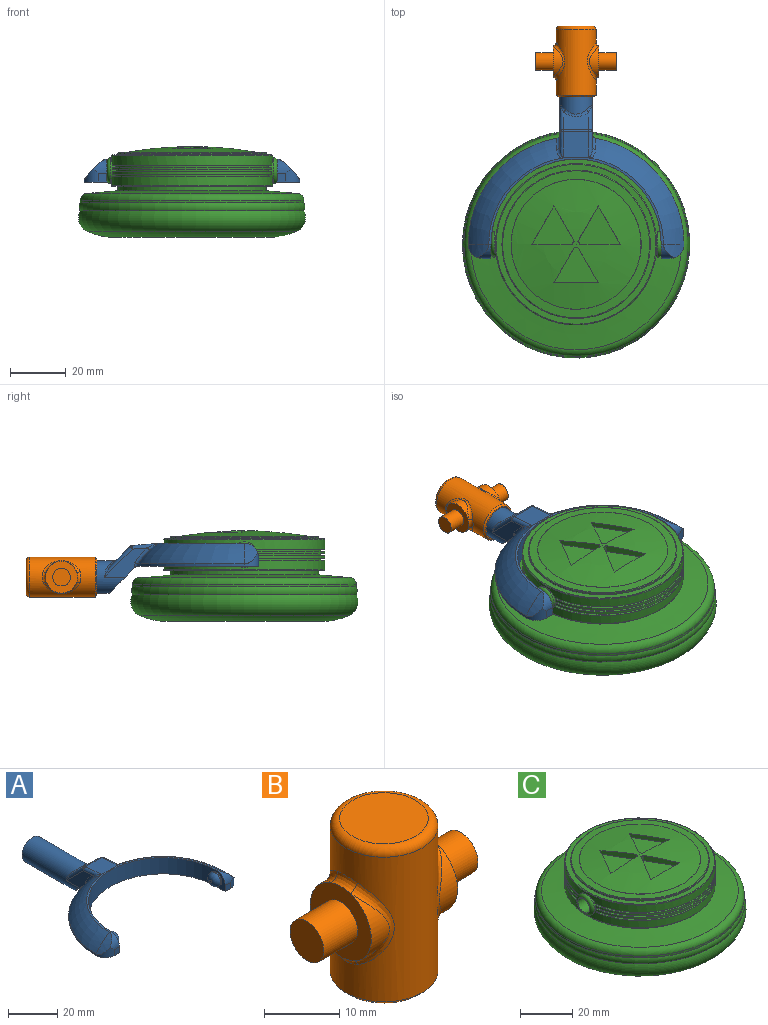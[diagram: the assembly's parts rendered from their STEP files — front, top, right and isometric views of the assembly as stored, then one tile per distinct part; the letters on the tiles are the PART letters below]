
ASSEMBLY  parts=3 mates=2
PART A: 48 faces, bbox 77.3x80.8x18.2 mm
  f0: plane 11.99x9.83mm, normal (0,-0.71,-0.71), area 141.5mm2, adj f1,f2,f9,f30,f43,f46
  f1: plane 15.39x10.49mm, normal (-1,0,0), area 63.5mm2, adj f0,f30,f32,f36,f46,f47
  f2: plane 15.39x10.49mm, normal (1,0,0), area 63.5mm2, adj f0,f30,f34,f39,f43,f44
  f3: plane 9.14x6.37mm, normal (0,0.71,0.71), area 67.6mm2, adj f35,f36,f39,f40
  f4: cylinder r=38.61mm len=37.99mm, axis (0,0,-1), area 42.6mm2, adj f6,f9,f17,f46,f47
  f5: torus R=19.3mm, axis (0,0,-1), area 507.8mm2, adj f10,f11,f12,f29,f42,f44
  f6: torus R=19.3mm, axis (0,0,-1), area 507.8mm2, adj f4,f11,f15,f28,f45,f47
  f7: cylinder r=30.48mm len=60.96mm, axis (0,0,-1), area 746.6mm2, adj f8,f9,f11,f14,f21,f24
  f8: plane 8.13x5.08mm, normal (-1,0,0), area 19.9mm2, adj f7,f9,f13,f19,f24
  f9: plane 77.22x43.73mm, normal (0,0,-1), area 956.2mm2, adj f0,f4,f7,f8,f10,f13,f14,f16
  f10: cylinder r=38.61mm len=37.99mm, axis (0,0,-1), area 42.6mm2, adj f5,f9,f20,f43,f44
  f11: plane 62.55x30.95mm, normal (0,0,1), area 75mm2, adj f5,f6,f7,f18,f19,f27
  f12: cylinder r=22.71mm len=7.33mm, axis (0,1,0), area 24.8mm2, adj f5,f19,f20
  f13: plane 3.05x3.05mm, normal (0,-1,0), area 9.3mm2, adj f8,f9,f19,f20
  f14: plane 8.13x5.08mm, normal (1,0,0), area 19.9mm2, adj f7,f9,f16,f18,f21
  f15: cylinder r=22.71mm len=7.33mm, axis (0,1,0), area 24.8mm2, adj f6,f17,f18
  f16: plane 3.05x3.05mm, normal (0,-1,0), area 9.3mm2, adj f9,f14,f17,f18
  f17: cylinder r=5.08mm len=5.08mm, axis (0,0,-1), area 21.9mm2, adj f4,f9,f15,f16,f18
  f18: cylinder r=5.08mm len=5.08mm, axis (-1,0,0), area 21.9mm2, adj f11,f14,f15,f16,f17
  f19: cylinder r=5.08mm len=5.08mm, axis (-1,0,0), area 21.9mm2, adj f8,f11,f12,f13,f20
  f20: cylinder r=5.08mm len=5.08mm, axis (0,0,-1), area 21.9mm2, adj f9,f10,f12,f13,f19
  f21: cylinder r=3.17mm len=6.35mm, axis (-1,0,0), area 12.7mm2, adj f7,f14,f23
  f22: plane 1.27x1.27mm, normal (1,0,0), area 1.3mm2, adj f23
  f23: torus R=0.64mm, axis (1,0,0), area 56.5mm2, adj f21,f22
  f24: cylinder r=3.17mm len=6.35mm, axis (1,0,0), area 12.7mm2, adj f7,f8,f26
  f25: plane 1.27x1.27mm, normal (-1,0,0), area 1.3mm2, adj f26
  f26: torus R=0.64mm, axis (-1,0,0), area 56.5mm2, adj f24,f25
  f27: plane 9.86x9.36mm, normal (0,0.09,1), area 85.6mm2, adj f11,f28,f29,f32,f34,f35,f42,f45
  f28: plane 1.04x0.17mm, normal (0,-1,0), area 0mm2, adj f6,f27,f45
  f29: plane 1.04x0.17mm, normal (0,-1,0), area 0mm2, adj f5,f27,f42
  f30: cylinder r=5.84mm len=33.01mm, axis (0,-1,0), area 1029.7mm2, adj f0,f1,f2,f31,f38,f40,f41
  f31: plane 11.68x11.68mm, normal (0,1,0), area 107.2mm2, adj f30
  f32: cylinder r=1.27mm len=9.13mm, axis (0,-1,0.09), area 14.4mm2, adj f1,f27,f33,f45
  f33: sphere r=1.27mm, area 1.5mm2, adj f32,f35,f36
  f34: cylinder r=1.27mm len=9.13mm, axis (0,1,-0.09), area 14.4mm2, adj f2,f27,f37,f42
  f35: cylinder r=1.27mm len=9.14mm, axis (-1,0,0), area 8.1mm2, adj f3,f27,f33,f37
  f36: cylinder r=1.27mm len=10.91mm, axis (0,-0.71,0.71), area 23.1mm2, adj f1,f3,f33,f38
  f37: sphere r=1.27mm, area 1.5mm2, adj f34,f35,f39
  f38: bspline ~4.55x2.75mm, area 2.3mm2, adj f30,f36,f40
  f39: cylinder r=1.27mm len=10.91mm, axis (0,0.71,-0.71), area 23.1mm2, adj f2,f3,f37,f41
  f40: bspline ~9.14x2.56mm, area 10.7mm2, adj f3,f30,f38,f41
  f41: bspline ~5.23x3.53mm, area 2.3mm2, adj f30,f39,f40
  f42: bspline ~4.62x3.14mm, area 5.2mm2, adj f5,f27,f29,f34,f44
  f43: cylinder r=1.27mm len=1.74mm, axis (0,0,-1), area 1.9mm2, adj f0,f2,f9,f10,f44
  f44: bspline ~8.6x7.86mm, area 11.9mm2, adj f2,f5,f10,f42,f43
  f45: bspline ~4.62x3.14mm, area 5.2mm2, adj f6,f27,f28,f32,f47
  f46: cylinder r=1.27mm len=1.74mm, axis (0,0,-1), area 1.9mm2, adj f0,f1,f4,f9,f47
  f47: bspline ~8.6x7.86mm, area 11.9mm2, adj f1,f4,f6,f45,f46
PART B: 25 faces, bbox 28.9x15.5x25.4 mm
  f0: cylinder r=5.71mm len=10.81mm, axis (-1,0,0), area 26.2mm2, adj f5,f15
  f1: cylinder r=5.71mm len=10.81mm, axis (-1,0,0), area 26.2mm2, adj f8,f11
  f2: cylinder r=7.14mm len=23.5mm, axis (0,0,-1), area 763.2mm2, adj f9,f10,f11,f12,f13,f14,f15,f16
  f3: plane 11.75x11.75mm, normal (0,0,1), area 108.4mm2, adj f17
  f4: plane 13.02x13.02mm, normal (0,0,-1), area 16.3mm2, adj f22,f24
  f5: plane 11.46x11.46mm, normal (1,0,0), area 70.9mm2, adj f0,f6,f13,f16,f18
  f6: cylinder r=5.71mm len=10.81mm, axis (-1,0,0), area 26.2mm2, adj f5,f14
  f7: cylinder r=5.71mm len=10.81mm, axis (-1,0,0), area 26.2mm2, adj f8,f10
  f8: plane 11.46x11.46mm, normal (-1,0,0), area 70.9mm2, adj f1,f7,f9,f12,f20
  f9: bspline ~4.64x1.73mm, area 6.5mm2, adj f2,f8,f10,f11
  f10: bspline ~13.62x4.91mm, area 20.7mm2, adj f2,f7,f9,f12
  f11: bspline ~13.6x4.87mm, area 20.7mm2, adj f1,f2,f9,f12
  f12: bspline ~4.64x1.73mm, area 6.5mm2, adj f2,f8,f10,f11
  f13: bspline ~4.64x1.73mm, area 6.5mm2, adj f2,f5,f14,f15
  f14: bspline ~13.62x4.91mm, area 20.7mm2, adj f2,f6,f13,f16
  f15: bspline ~13.6x4.87mm, area 20.7mm2, adj f0,f2,f13,f16
  f16: bspline ~4.64x1.73mm, area 6.5mm2, adj f2,f5,f14,f15
  f17: torus R=5.87mm, axis (0,0,1), area 83.8mm2, adj f2,f3
  f18: cylinder r=3.17mm len=6.35mm, axis (-1,0,0), area 126.7mm2, adj f5,f19
  f19: plane 6.35x6.35mm, normal (1,0,0), area 31.7mm2, adj f18
  f20: cylinder r=3.17mm len=6.35mm, axis (1,0,0), area 126.7mm2, adj f8,f21
  f21: plane 6.35x6.35mm, normal (-1,0,0), area 31.7mm2, adj f20
  f22: cylinder r=6.1mm len=22.86mm, axis (0,0,-1), area 875.6mm2, adj f4,f23
  f23: plane 12.19x12.19mm, normal (0,0,-1), area 116.7mm2, adj f22
  f24: cone r=7.14mm half-angle=45deg, axis (0,0,1), area 38.5mm2, adj f2,f4
PART C: 64 faces, bbox 96.2x96.2x32.5 mm
  f0: sphere r=135.39mm, area 1385.3mm2, adj f48,f49,f50,f51,f52,f54,f55,f56
  f1: cylinder r=28.87mm len=57.73mm, axis (0,0,-1), area 595.7mm2, adj f2,f3,f39,f40,f45
  f2: plane 57.13x24.71mm, normal (0,0,1), area 102mm2, adj f1,f4,f39,f40
  f3: plane 57.13x24.71mm, normal (0,0,1), area 102mm2, adj f1,f5,f39,f40
  f4: cylinder r=27.6mm len=54.56mm, axis (0,0,1), area 49.6mm2, adj f2,f7,f39,f40
  f5: cylinder r=27.6mm len=54.56mm, axis (0,0,1), area 49.6mm2, adj f3,f6,f39,f40
  f6: plane 57.06x24.48mm, normal (0,0,-1), area 101.4mm2, adj f5,f8,f39,f40
  f7: plane 57.06x24.48mm, normal (0,0,-1), area 101.4mm2, adj f4,f9,f39,f40
  f8: cylinder r=28.87mm len=57.06mm, axis (0,0,-1), area 77.8mm2, adj f6,f13,f39,f40
  f9: cylinder r=28.87mm len=57.06mm, axis (0,0,-1), area 77.8mm2, adj f7,f12,f39,f40
  f10: plane 57.01x24.31mm, normal (0,0,-1), area 101mm2, adj f15,f16,f39,f40
  f11: plane 57.01x24.31mm, normal (0,0,-1), area 101mm2, adj f14,f17,f39,f40
  f12: plane 57.01x24.31mm, normal (0,0,1), area 101mm2, adj f9,f14,f39,f40
  f13: plane 57.01x24.31mm, normal (0,0,1), area 101mm2, adj f8,f15,f39,f40
  f14: cylinder r=27.6mm len=54.44mm, axis (0,0,1), area 49.2mm2, adj f11,f12,f39,f40
  f15: cylinder r=27.6mm len=54.44mm, axis (0,0,1), area 49.2mm2, adj f10,f13,f39,f40
  f16: cylinder r=28.87mm len=57.06mm, axis (0,0,-1), area 77.8mm2, adj f10,f20,f39,f40
  f17: cylinder r=28.87mm len=57.06mm, axis (0,0,-1), area 77.8mm2, adj f11,f21,f39,f40
  f18: plane 57.13x24.71mm, normal (0,0,-1), area 102mm2, adj f22,f24,f39,f40
  f19: plane 57.13x24.71mm, normal (0,0,-1), area 102mm2, adj f23,f24,f39,f40
  f20: plane 57.06x24.48mm, normal (0,0,1), area 101.4mm2, adj f16,f23,f39,f40
  f21: plane 57.06x24.48mm, normal (0,0,1), area 101.4mm2, adj f17,f22,f39,f40
  f22: cylinder r=27.6mm len=54.56mm, axis (0,0,1), area 49.6mm2, adj f18,f21,f39,f40
  f23: cylinder r=27.6mm len=54.56mm, axis (0,0,1), area 49.6mm2, adj f19,f20,f39,f40
  f24: cylinder r=28.87mm len=57.73mm, axis (0,0,-1), area 595.8mm2, adj f18,f19,f39,f40,f46
  f25: plane 39.33x39.33mm, normal (0,0,-1), area 1214.6mm2, adj f26
  f26: torus R=20.12mm, axis (0,0,-1), area 1429.3mm2, adj f25,f27
  f27: torus R=27.74mm, axis (0,0,-1), area 3542.1mm2, adj f26,f28
  f28: torus R=35.36mm, axis (0,0,-1), area 2180.1mm2, adj f27,f29
  f29: torus R=37.35mm, axis (0,0,-1), area 734.6mm2, adj f28,f30
  f30: cylinder r=40.06mm len=80.11mm, axis (0,0,-1), area 213.3mm2, adj f29,f34
  f31: cone r=26.57mm half-angle=85deg, axis (0,0,-1), area 2265mm2, adj f32,f34
  f32: cylinder r=26.57mm len=53.14mm, axis (0,0,-1), area 265mm2, adj f31,f33
  f33: plane 57.23x57.23mm, normal (0,0,-1), area 354.5mm2, adj f32,f45
  f34: torus R=37.52mm, axis (0,0,1), area 928.6mm2, adj f30,f31
  f35: cone r=26.57mm half-angle=87deg, axis (0,0,-1), area 475.4mm2, adj f47,f48
  f36: cylinder r=26.57mm len=53.14mm, axis (0,0,-1), area 92.3mm2, adj f37,f47
  f37: plane 57.23x57.23mm, normal (0,0,1), area 354.5mm2, adj f36,f46
  f38: plane 6.6x6.6mm, normal (1,0,0), area 2.6mm2, adj f43,f44
  f39: cylinder r=4.57mm len=9.14mm, axis (-1,0,0), area 20.2mm2, adj f1,f2,f3,f4,f5,f6,f7,f8
  f40: cylinder r=4.57mm len=9.14mm, axis (-1,0,0), area 20.2mm2, adj f1,f2,f3,f4,f5,f6,f7,f8
  f41: plane 6.6x6.6mm, normal (-1,0,0), area 2.6mm2, adj f42,f44
  f42: torus R=3.3mm, axis (1,0,0), area 51.5mm2, adj f40,f41
  f43: torus R=3.3mm, axis (1,0,0), area 51.5mm2, adj f38,f39
  f44: cylinder r=3.17mm len=60.96mm, axis (1,0,0), area 1216.1mm2, adj f38,f41
  f45: torus R=28.61mm, axis (0,0,1), area 72.1mm2, adj f1,f33
  f46: torus R=28.61mm, axis (0,0,-1), area 72.1mm2, adj f24,f37
  f47: torus R=26.31mm, axis (0,0,1), area 64.2mm2, adj f35,f36
  f48: torus R=23.29mm, axis (0,0,1), area 4.5mm2, adj f0,f35
  f49: cylinder r=1.27mm len=2.53mm, axis (0,0,1), area 3.4mm2, adj f0,f50,f52,f53
  f50: plane 12.65x7.3mm, normal (-0.87,-0.5,0), area 32.2mm2, adj f0,f49,f51,f53
  f51: plane 13.75x7.94mm, normal (0.87,-0.5,0), area 28mm2, adj f0,f50,f52,f53
  f52: plane 14.61x2.53mm, normal (0,1,0), area 32.2mm2, adj f0,f49,f51,f53
  f53: plane 15.24x13.75mm, normal (0,0,1), area 108.3mm2, adj f49,f50,f51,f52
  f54: cylinder r=1.27mm len=2.53mm, axis (0,0,1), area 3.4mm2, adj f0,f55,f57,f58
  f55: plane 14.61x2.53mm, normal (0,1,0), area 32.2mm2, adj f0,f54,f56,f58
  f56: plane 13.75x7.94mm, normal (-0.87,-0.5,0), area 28mm2, adj f0,f55,f57,f58
  f57: plane 12.65x7.3mm, normal (0.87,-0.5,0), area 32.2mm2, adj f0,f54,f56,f58
  f58: plane 15.24x13.75mm, normal (0,0,1), area 108.3mm2, adj f54,f55,f56,f57
  f59: plane 15.88x1.84mm, normal (0,1,0), area 28mm2, adj f0,f60,f62,f63
  f60: plane 12.65x7.3mm, normal (-0.87,-0.5,0), area 32.2mm2, adj f0,f59,f61,f63
  f61: cylinder r=1.27mm len=2.53mm, axis (0,0,1), area 3.4mm2, adj f0,f60,f62,f63
  f62: plane 12.65x7.3mm, normal (0.87,-0.5,0), area 32.2mm2, adj f0,f59,f61,f63
  f63: plane 15.88x12.65mm, normal (0,0,1), area 108.3mm2, adj f59,f60,f61,f62
PLACE A t=(32.34,27.52,20.85)mm
PLACE B rot(axis=(-1,0,0),90deg) t=(32.34,80.3,16.88)mm
PLACE C t=(32.34,27.52,33.52)mm
MATE revolute A.f24 <-> C.f39  axis (-1,0,0) through (62.82,27.52,24.92)mm
MATE revolute B.f2 <-> A.f30  axis (0,-1,0) through (32.34,103.16,16.88)mm
